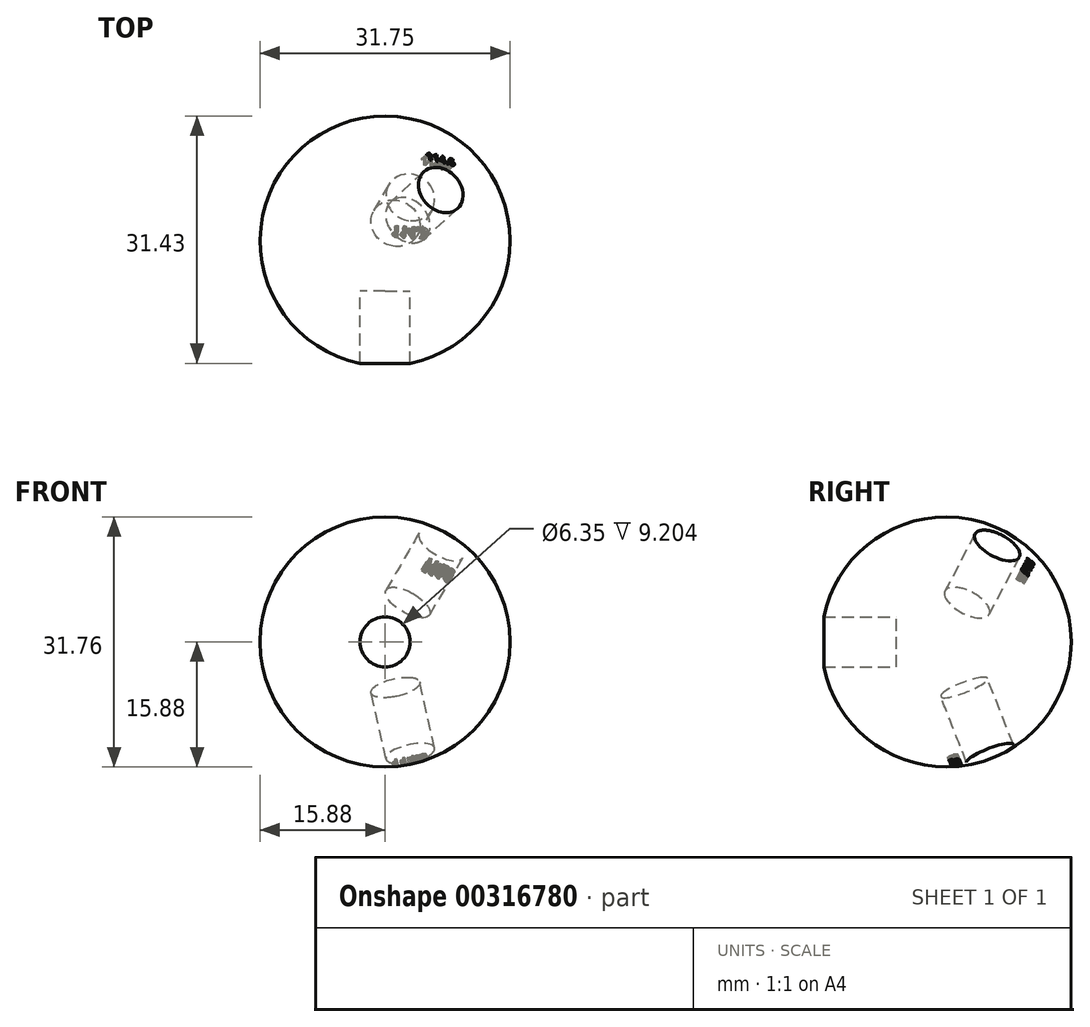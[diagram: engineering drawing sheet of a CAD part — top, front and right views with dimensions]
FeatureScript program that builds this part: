
annotation { "Feature Type Name" : "Feature", "Feature Type Description" : "" }
export const myFeature = defineFeature(function(context is Context, id is Id, definition is map)
    precondition{}
    {
        {
            var Q0;
            Q0=qCreatedBy(makeId("Front.planeOp"),FACE);
            var sketch = newSketch(context, id + "F0", { "sketchPlane" : qUnion([Q0])});
            skArc(sketch, "E0", {"start": v(0, 15.88) * mm, "mid": v(-15.88, 0) * mm, "end": v(0, -15.88) * mm});
            skLineSegment(sketch, "E1", {"start": v(0, 15.88) * mm, "end": v(0, -15.88) * mm});
            skSolve(sketch);
        }
        {
            var Q0;
            Q0=qCreatedBy(makeId("Top.planeOp"),FACE);
            var sketch = newSketch(context, id + "F1", { "sketchPlane" : qUnion([Q0])});
            skCircle(sketch, "E2", {"center": v(0, 0) * mm, "radius": 15.88 * mm});
            skSolve(sketch);
        }
        {
            var Q0;
            Q0=makeQuery(id+"F0.imprint","IMPRINT",FACE,{"disambiguationData":[TD([[makeQuery(id+"F0.imprint","IMPRINT",EDGE,{"derivedFrom":sQuery(id+"F0.wireOp",EDGE,"E0")}),1.0]])]});
            var Q1;
            Q1=sQuery(id+"F1.wireOp",EDGE,"E2");
            revolve(context, id + "F2", {"entities" : qUnion([Q0]), "axis" : qUnion([Q1]), "revolveType" : RevolveType.FULL});
        }
        {
            var Q0;
            Q0=qCreatedBy(makeId("Front.planeOp"),FACE);
            cPlane(context, id + "F3", {"entities" : qUnion([Q0]), "cplaneType" : CPlaneType.OFFSET, "offset" : 6.35 * mm, "width" : 152.4 * mm, "height" : 152.4 * mm});
        }
        {
            var Q0;
            Q0=qCreatedBy(id+"F3.planeOp",FACE);
            var sketch = newSketch(context, id + "F4", { "sketchPlane" : qUnion([Q0])});
            skCircle(sketch, "E3", {"center": v(0, 0) * mm, "radius": 3.18 * mm});
            skSolve(sketch);
        }
        {
            var Q0;
            Q0=qSketchRegion(id+"F4",true);
            extrude(context, id + "F5", {"entities" : qUnion([Q0]), "depth" : 19.05 * mm});
        }
        {
            var Q0;
            Q0=qCreatedBy(makeId("Top.planeOp"),FACE);
            var sketch = newSketch(context, id + "F6", { "sketchPlane" : qUnion([Q0])});
            skLineSegment(sketch, "E4", {"start": v(0, 42.4) * mm, "end": v(0, -56.04) * mm, "construction": true});
            skSolve(sketch);
        }
        {
            var Q0;
            Q0=qCreatedBy(makeId("Top.planeOp"),FACE);
            var sketch = newSketch(context, id + "F7", { "sketchPlane" : qUnion([Q0])});
            skLineSegment(sketch, "E5", {"start": v(-57.15, 0) * mm, "end": v(49.96, 0) * mm, "construction": true});
            skSolve(sketch);
        }
        {
            var Q0;
            Q0=qCreatedBy(makeId("Front.planeOp"),FACE);
            var sketch = newSketch(context, id + "F8", { "sketchPlane" : qUnion([Q0])});
            skLineSegment(sketch, "E6", {"start": v(0, 36.5) * mm, "end": v(0, -44.06) * mm, "construction": true});
            skSolve(sketch);
        }
        {
            var Q0;
            Q0=makeQuery(id+"F5.opExtrude","SWEPT_BODY",BODY,{"disambiguationData":[OSD([sQuery(id+"F4.wireOp",EDGE,"E3")])]});
            var Q1;
            Q1=sQuery(id+"F8.wireOp",EDGE,"E6");
            var Q2;
            Q2=sQuery(id+"F7.wireOp",EDGE,"E5");
            transform(context, id + "F9", {"entities" : qUnion([Q0]), "transformType" : TransformType.ROTATION, "transformAxis" : qUnion([Q2]), "angle" : 114.3 * degree, "makeCopy" : true});
        }
        {
            var Q0;
            Q0=makeQuery(id+"F5.opExtrude","SWEPT_BODY",BODY,{"disambiguationData":[OSD([sQuery(id+"F4.wireOp",EDGE,"E3")])]});
            var Q1;
            Q1=sQuery(id+"F7.wireOp",EDGE,"E5");
            transform(context, id + "F10", {"entities" : qUnion([Q0]), "transformType" : TransformType.ROTATION, "transformAxis" : qUnion([Q1]), "angle" : 114.6 * degree, "oppositeDirection" : true, "makeCopy" : true});
        }
        {
            var Q0;
            Q0=makeQuery(id+"F10.opPattern","COPY",BODY,{"derivedFrom":makeQuery(id+"F5.opExtrude","SWEPT_BODY",BODY,{"disambiguationData":[OSD([sQuery(id+"F4.wireOp",EDGE,"E3")])]}),"instanceName":"1"});
            var Q1;
            Q1=sQuery(id+"F6.wireOp",EDGE,"E4");
            transform(context, id + "F11", {"entities" : qUnion([Q0]), "transformType" : TransformType.ROTATION, "transformAxis" : qUnion([Q1]), "angle" : 30 * degree, "oppositeDirection" : true, "makeCopy" : false});
        }
        {
            var Q0;
            Q0=makeQuery(id+"F9.opPattern","COPY",BODY,{"derivedFrom":makeQuery(id+"F5.opExtrude","SWEPT_BODY",BODY,{"disambiguationData":[OSD([sQuery(id+"F4.wireOp",EDGE,"E3")])]}),"instanceName":"1"});
            var Q1;
            Q1=sQuery(id+"F8.wireOp",EDGE,"E6");
            transform(context, id + "F12", {"entities" : qUnion([Q0]), "transformType" : TransformType.ROTATION, "transformAxis" : qUnion([Q1]), "angle" : 30 * degree, "makeCopy" : false});
        }
        {
            var Q0;
            Q0=makeQuery(id+"F10.opPattern","COPY",FACE,{"derivedFrom":makeQuery(id+"F5.opExtrude","CAP_FACE",FACE,{"disambiguationData":[OSD([sQuery(id+"F4.wireOp",EDGE,"E3")])],"isStart":false}),"instanceName":"1"});
            cPlane(context, id + "F13", {"entities" : qUnion([Q0]), "cplaneType" : CPlaneType.OFFSET, "offset" : 8 * mm, "oppositeDirection" : true, "width" : 152.4 * mm, "height" : 152.4 * mm});
        }
        {
            var Q0;
            Q0=makeQuery(id+"F9.opPattern","COPY",FACE,{"derivedFrom":makeQuery(id+"F5.opExtrude","CAP_FACE",FACE,{"disambiguationData":[OSD([sQuery(id+"F4.wireOp",EDGE,"E3")])],"isStart":false}),"instanceName":"1"});
            cPlane(context, id + "F14", {"entities" : qUnion([Q0]), "cplaneType" : CPlaneType.OFFSET, "offset" : 7.62 * mm, "oppositeDirection" : true, "width" : 152.4 * mm, "height" : 152.4 * mm});
        }
        {
            var Q0;
            Q0=qCreatedBy(id+"F13.planeOp",FACE);
            var sketch = newSketch(context, id + "F15", { "sketchPlane" : qUnion([Q0])});
            skText(sketch, "E7", { "text": "114.6\n", "fontName": "OpenSans-Bold.ttf"});
            const initialGuessF15  = {"E7": [-0.00183, 0.00414, 1, 0, 0.00114]};
            skSetInitialGuess(sketch, initialGuessF15);
            skSolve(sketch);
        }
        {
            var Q0;
            Q0=qSketchRegion(id+"F15",true);
            extrude(context, id + "F16", {"entities" : qUnion([Q0]), "operationType" : NewBodyOperationType.REMOVE, "oppositeDirection" : true, "depth" : 3.76 * mm});
        }
        {
            var Q0;
            Q0=qCreatedBy(id+"F14.planeOp",FACE);
            var sketch = newSketch(context, id + "F17", { "sketchPlane" : qUnion([Q0])});
            skText(sketch, "E8", { "text": "114.3", "fontName": "OpenSans-Bold.ttf"});
            const initialGuessF17  = {"E8": [-0.00227, 0.00387, 1, 0, 0.0013]};
            skSetInitialGuess(sketch, initialGuessF17);
            skSolve(sketch);
        }
        {
            var Q0;
            Q0=qSketchRegion(id+"F17",true);
            extrude(context, id + "F18", {"entities" : qUnion([Q0]), "operationType" : NewBodyOperationType.REMOVE, "oppositeDirection" : true, "depth" : 3.33 * mm});
        }
        {
            var Q0;
            Q0=makeQuery(id+"F5.opExtrude","SWEPT_BODY",BODY,{"disambiguationData":[OSD([sQuery(id+"F4.wireOp",EDGE,"E3")])]});
            var Q1;
            Q1=makeQuery(id+"F2.opRevolve","SWEPT_BODY",BODY,{"disambiguationData":[OSD([sQuery(id+"F0.wireOp",EDGE,"E0"),sQuery(id+"F0.wireOp",EDGE,"E1")])]});
            booleanBodies(context, id + "F19", {"operationType" : BooleanOperationType.SUBTRACTION, "tools" : qUnion([Q0]), "targets" : qUnion([Q1])});
        }
        {
            var Q0;
            Q0=makeQuery(id+"F10.opPattern","COPY",BODY,{"derivedFrom":makeQuery(id+"F5.opExtrude","SWEPT_BODY",BODY,{"disambiguationData":[OSD([sQuery(id+"F4.wireOp",EDGE,"E3")])]}),"instanceName":"1"});
            var Q1;
            Q1=makeQuery(id+"F2.opRevolve","SWEPT_BODY",BODY,{"disambiguationData":[OSD([sQuery(id+"F0.wireOp",EDGE,"E0"),sQuery(id+"F0.wireOp",EDGE,"E1")])]});
            booleanBodies(context, id + "F20", {"operationType" : BooleanOperationType.SUBTRACTION, "tools" : qUnion([Q0]), "targets" : qUnion([Q1])});
        }
        {
            var Q0;
            Q0=makeQuery(id+"F9.opPattern","COPY",BODY,{"derivedFrom":makeQuery(id+"F5.opExtrude","SWEPT_BODY",BODY,{"disambiguationData":[OSD([sQuery(id+"F4.wireOp",EDGE,"E3")])]}),"instanceName":"1"});
            var Q1;
            Q1=makeQuery(id+"F2.opRevolve","SWEPT_BODY",BODY,{"disambiguationData":[OSD([sQuery(id+"F0.wireOp",EDGE,"E0"),sQuery(id+"F0.wireOp",EDGE,"E1")])]});
            booleanBodies(context, id + "F21", {"operationType" : BooleanOperationType.SUBTRACTION, "tools" : qUnion([Q0]), "targets" : qUnion([Q1])});
        }
    });
